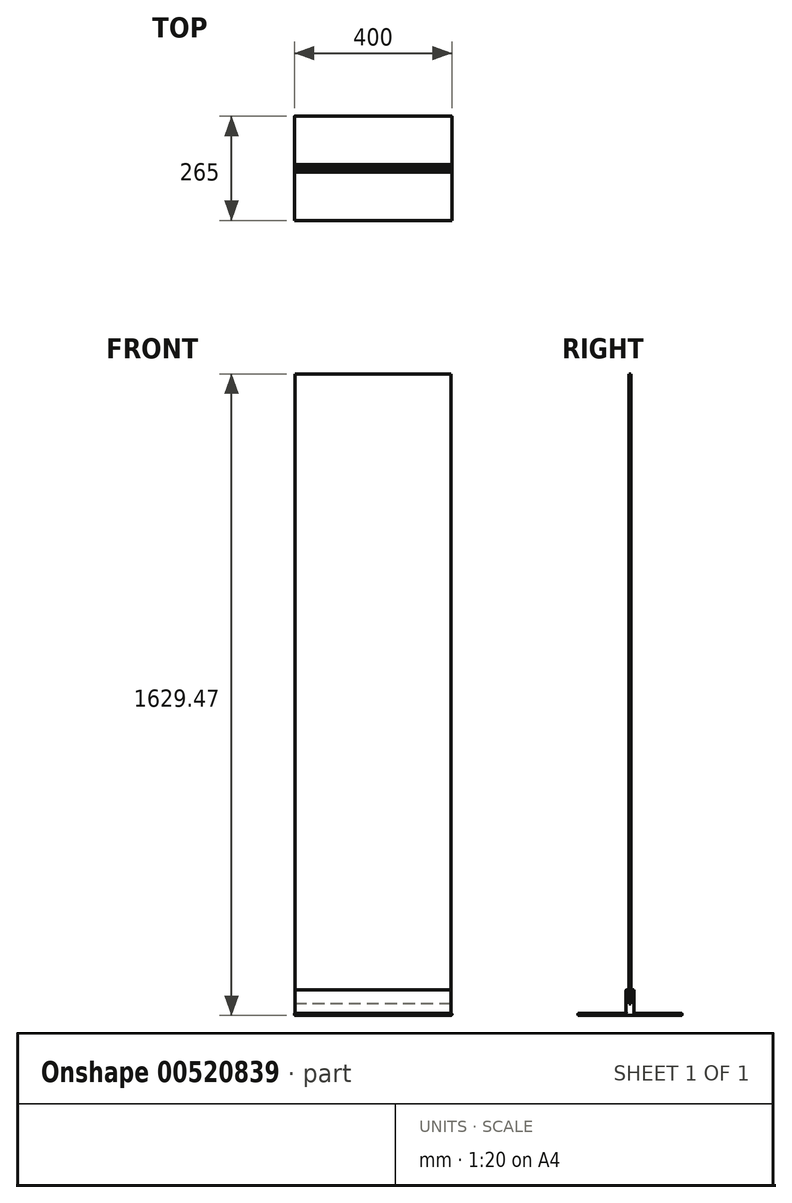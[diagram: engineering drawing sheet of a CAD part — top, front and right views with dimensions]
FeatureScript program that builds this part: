
annotation { "Feature Type Name" : "Feature", "Feature Type Description" : "" }
export const myFeature = defineFeature(function(context is Context, id is Id, definition is map)
    precondition{}
    {
        {
            var Q0;
            Q0=qCreatedBy(makeId("Top.planeOp"),FACE);
            var sketch = newSketch(context, id + "F0", { "sketchPlane" : qUnion([Q0])});
            skLineSegment(sketch, "E0.bottom", {"start": v(0, 0) * mm, "end": v(400, 0) * mm});
            skLineSegment(sketch, "E0.top", {"start": v(0, 265) * mm, "end": v(400, 265) * mm});
            skLineSegment(sketch, "E0.left", {"start": v(0, 0) * mm, "end": v(0, 265) * mm});
            skLineSegment(sketch, "E0.right", {"start": v(400, 0) * mm, "end": v(400, 265) * mm});
            skSolve(sketch);
        }
        {
            var Q0;
            Q0 = qSketchRegion(id + "F0", true);
            extrude(context, id + "F1", {"entities" : qUnion([Q0]), "depth" : 5 * mm, "offsetDistance" : 25 * mm});
        }
        {
            var Q0;
            Q0=makeQuery(id+"F1.opExtrude","CAP_FACE",FACE,{"disambiguationData":[OSD([sQuery(id+"F0.wireOp",EDGE,"E0.bottom"),sQuery(id+"F0.wireOp",EDGE,"E0.top"),sQuery(id+"F0.wireOp",EDGE,"E0.left"),sQuery(id+"F0.wireOp",EDGE,"E0.right")])],"isStart":false});
            fillet(context, id + "F2", {"entities" : qUnion([Q0]), "radius" : 2 * mm, "tangentPropagation" : true, "allowEdgeOverflow" : false});
        }
        {
            var Q0;
            Q0=makeQuery(id+"F1.opExtrude","CAP_FACE",FACE,{"disambiguationData":[OSD([sQuery(id+"F0.wireOp",EDGE,"E0.bottom"),sQuery(id+"F0.wireOp",EDGE,"E0.top"),sQuery(id+"F0.wireOp",EDGE,"E0.left"),sQuery(id+"F0.wireOp",EDGE,"E0.right")])],"isStart":false});
            var sketch = newSketch(context, id + "F3", { "sketchPlane" : qUnion([Q0])});
            skLineSegment(sketch, "E1", {"start": v(2, 132.5) * mm, "end": v(398, 132.5) * mm, "construction": true});
            skLineSegment(sketch, "E2.bottom", {"start": v(2, 142.5) * mm, "end": v(398, 142.5) * mm});
            skLineSegment(sketch, "E2.top", {"start": v(2, 122.5) * mm, "end": v(398, 122.5) * mm});
            skLineSegment(sketch, "E2.left", {"start": v(2, 142.5) * mm, "end": v(2, 122.5) * mm});
            skLineSegment(sketch, "E2.right", {"start": v(398, 142.5) * mm, "end": v(398, 122.5) * mm});
            skSolve(sketch);
        }
        {
            var Q0;
            Q0 = qSketchRegion(id + "F3", true);
            extrude(context, id + "F4", {"entities" : qUnion([Q0]), "operationType" : NewBodyOperationType.ADD, "depth" : 60 * mm, "offsetDistance" : 25 * mm});
        }
        {
            var Q0;
            Q0=makeQuery(id+"F4.opExtrude","SWEPT_FACE",FACE,{"disambiguationData":[OSD([sQuery(id+"F3.wireOp",EDGE,"E2.top")])]});
            var Q1;
            Q1=makeQuery(id+"F4.opExtrude","CAP_FACE",FACE,{"disambiguationData":[OSD([sQuery(id+"F3.wireOp",EDGE,"E2.bottom"),sQuery(id+"F3.wireOp",EDGE,"E2.top"),sQuery(id+"F3.wireOp",EDGE,"E2.left"),sQuery(id+"F3.wireOp",EDGE,"E2.right")])],"isStart":false});
            var Q2;
            Q2=makeQuery(id+"F4.opExtrude","SWEPT_FACE",FACE,{"disambiguationData":[OSD([sQuery(id+"F3.wireOp",EDGE,"E2.bottom")])]});
            var Q3;
            Q3=makeQuery(id+"F4.opExtrude","SWEPT_FACE",FACE,{"disambiguationData":[OSD([sQuery(id+"F3.wireOp",EDGE,"E2.right")])]});
            var Q4;
            Q4=makeQuery(id+"F1.opExtrude","CAP_FACE",FACE,{"disambiguationData":[OSD([sQuery(id+"F0.wireOp",EDGE,"E0.bottom"),sQuery(id+"F0.wireOp",EDGE,"E0.top"),sQuery(id+"F0.wireOp",EDGE,"E0.left"),sQuery(id+"F0.wireOp",EDGE,"E0.right")])],"isStart":true});
            var Q5;
            Q5=makeQuery(id+"F4.opExtrude","SWEPT_FACE",FACE,{"disambiguationData":[OSD([sQuery(id+"F3.wireOp",EDGE,"E2.left")])]});
            fillet(context, id + "F5", {"entities" : qUnion([Q0, Q1, Q2, Q3, Q4, Q5]), "radius" : 2 * mm, "tangentPropagation" : true, "allowEdgeOverflow" : false});
        }
        {
            var Q0;
            Q0=makeQuery(id+"F4.opExtrude","SWEPT_FACE",FACE,{"disambiguationData":[OSD([sQuery(id+"F3.wireOp",EDGE,"E2.left")])]});
            var sketch = newSketch(context, id + "F6", { "sketchPlane" : qUnion([Q0])});
            skLineSegment(sketch, "E3.left", {"start": v(-130, 66.42) * mm, "end": v(-130, 29.47) * mm});
            skLineSegment(sketch, "E3.right", {"start": v(-135, 66.42) * mm, "end": v(-135, 29.47) * mm});
            skLineSegment(sketch, "E4", {"start": v(-135, 66.42) * mm, "end": v(-130, 66.42) * mm});
            skLineSegment(sketch, "E5", {"start": v(-135, 29.47) * mm, "end": v(-130, 29.47) * mm});
            skSolve(sketch);
        }
        {
            var Q0;
            Q0 = qSketchRegion(id + "F6", true);
            var Q1;
            {var subQ8=sQuery(id+"F6.wireOp",EDGE,"E3.top");var subQ12=sQuery(id+"F6.wireOp",EDGE,"E3.left");var subQ13=makeQuery(id+"F6.imprint","INTERSECT",VERTEX,{"derivedFrom":[subQ8,subQ12]});Q1=makeQuery(id+"F6.imprint","IMPRINT",FACE,{"disambiguationData":[TD([[makeQuery(id+"F6.imprint","IMPRINT",EDGE,{"disambiguationData":[TD([[subQ13,-1.0]])],"derivedFrom":subQ8}),1.0]])]});}
            extrude(context, id + "F7", {"entities" : qUnion([Q0, Q1]), "operationType" : NewBodyOperationType.REMOVE, "endBound" : BoundingType.THROUGH_ALL, "oppositeDirection" : true, "depth" : 412 * mm, "offsetDistance" : 25 * mm});
        }
        {
            var Q0;
            Q0=makeQuery(id+"F7.boolean.opBoolean","COPY",FACE,{"derivedFrom":makeQuery(id+"F7.opExtrude","SWEPT_FACE",FACE,{"disambiguationData":[OSD([sQuery(id+"F6.wireOp",EDGE,"E5")])]})});
            var sketch = newSketch(context, id + "F8", { "sketchPlane" : qUnion([Q0])});
            skLineSegment(sketch, "E6.bottom", {"start": v(2, 135) * mm, "end": v(398, 135) * mm});
            skLineSegment(sketch, "E6.top", {"start": v(2, 130) * mm, "end": v(398, 130) * mm});
            skLineSegment(sketch, "E6.left", {"start": v(2, 135) * mm, "end": v(2, 130) * mm});
            skLineSegment(sketch, "E6.right", {"start": v(398, 135) * mm, "end": v(398, 130) * mm});
            skSolve(sketch);
        }
        {
            var Q0;
            Q0 = qSketchRegion(id + "F8", true);
            extrude(context, id + "F9", {"entities" : qUnion([Q0]), "depth" : 1600 * mm, "offsetDistance" : 25 * mm});
        }
    });
